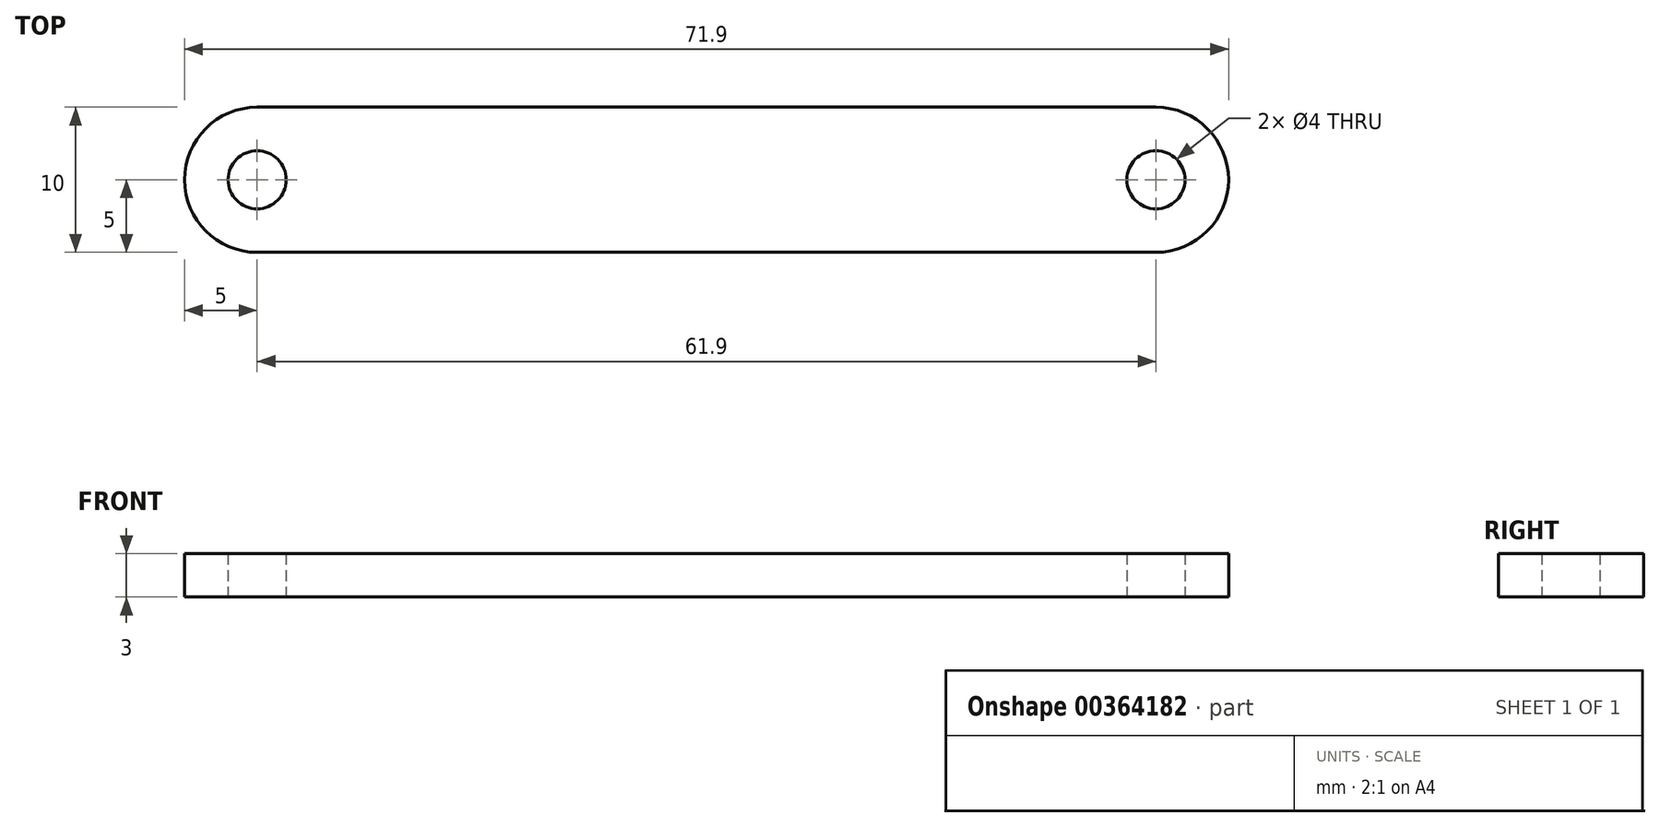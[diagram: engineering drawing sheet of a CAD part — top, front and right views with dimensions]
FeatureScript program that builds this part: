
annotation { "Feature Type Name" : "Feature", "Feature Type Description" : "" }
export const myFeature = defineFeature(function(context is Context, id is Id, definition is map)
    precondition{}
    {
        {
            var Q0;
            Q0=qCreatedBy(makeId("Top.planeOp"),FACE);
            var sketch = newSketch(context, id + "F0", { "sketchPlane" : qUnion([Q0])});
            skLineSegment(sketch, "E0.bottom", {"start": v(30.95, 5) * mm, "end": v(-30.95, 5) * mm});
            skLineSegment(sketch, "E0.top", {"start": v(30.95, -5) * mm, "end": v(-30.95, -5) * mm});
            skPoint(sketch, "E0.middle", {"position": v(0, 0) * mm});
            skCircle(sketch, "E1", {"center": v(-30.95, 0) * mm, "radius": 2 * mm});
            skCircle(sketch, "E2", {"center": v(30.95, 0) * mm, "radius": 2 * mm});
            skArc(sketch, "E3", {"start": v(-30.95, 5) * mm, "mid": v(-35.95, 0) * mm, "end": v(-30.95, -5) * mm});
            skArc(sketch, "E4", {"start": v(30.95, -5) * mm, "mid": v(35.95, 0) * mm, "end": v(30.95, 5) * mm});
            skSolve(sketch);
        }
        {
            var Q0;
            Q0=qSketchRegion(id+"F0",true);
            extrude(context, id + "F1", {"entities" : qUnion([Q0]), "depth" : 3 * mm});
        }
    });
